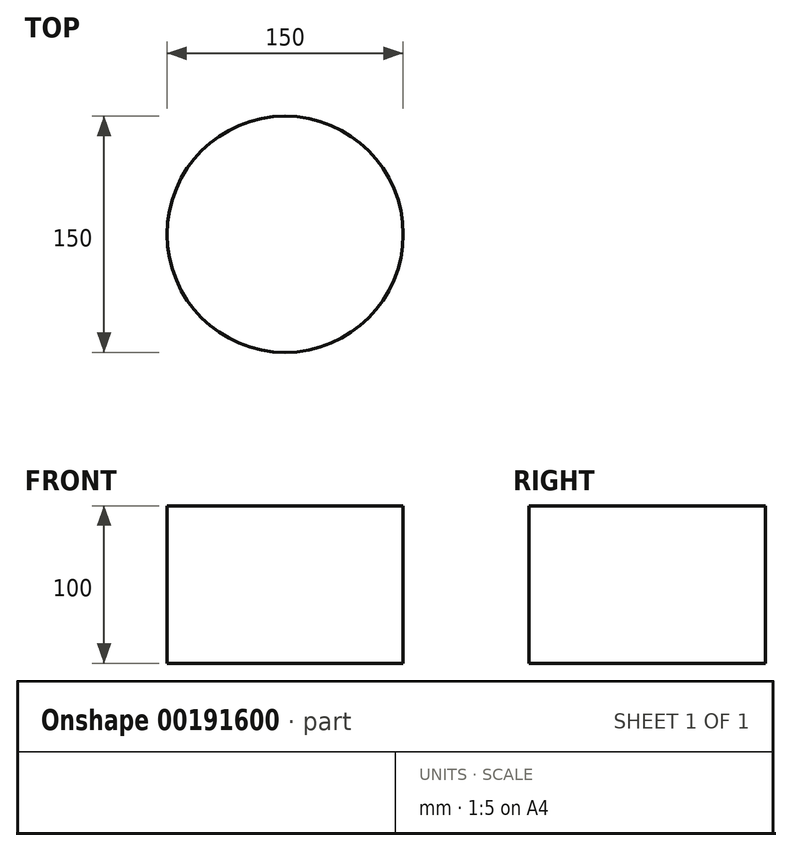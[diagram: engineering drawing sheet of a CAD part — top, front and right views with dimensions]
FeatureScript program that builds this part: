
annotation { "Feature Type Name" : "Feature", "Feature Type Description" : "" }
export const myFeature = defineFeature(function(context is Context, id is Id, definition is map)
    precondition{}
    {
        {
            var Q0;
            Q0=qCreatedBy(makeId("Top.planeOp"),FACE);
            var sketch = newSketch(context, id + "F0", { "sketchPlane" : qUnion([Q0])});
            skCircle(sketch, "E0", {"center": v(0, 0) * mm, "radius": 75 * mm});
            skSolve(sketch);
        }
        {
            var Q0;
            Q0=makeQuery(id+"F0.imprint","IMPRINT",FACE,{"disambiguationData":[TD([[makeQuery(id+"F0.imprint","IMPRINT",EDGE,{"derivedFrom":sQuery(id+"F0.wireOp",EDGE,"E0")}),1.0]])]});
            extrude(context, id + "F1", {"entities" : qUnion([Q0]), "depth" : 100 * mm});
        }
    });
